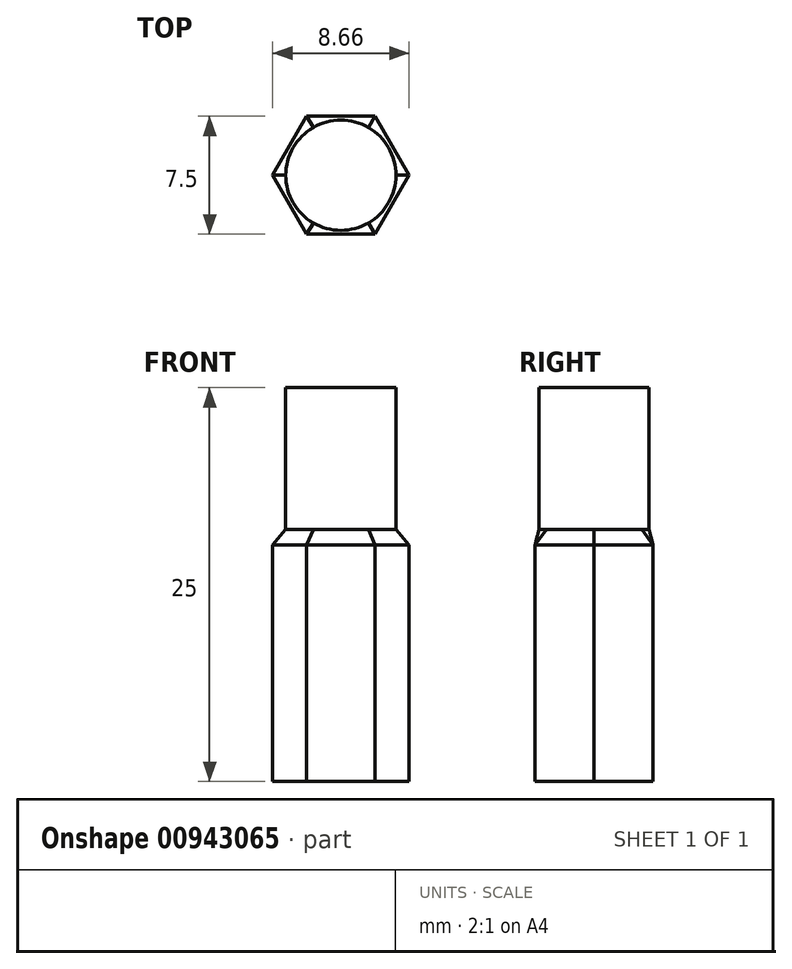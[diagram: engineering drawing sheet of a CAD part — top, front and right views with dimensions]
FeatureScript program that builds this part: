
annotation { "Feature Type Name" : "Feature", "Feature Type Description" : "" }
export const myFeature = defineFeature(function(context is Context, id is Id, definition is map)
    precondition{}
    {
        {
            var Q0;
            Q0=qCreatedBy(makeId("Top.planeOp"),FACE);
            var sketch = newSketch(context, id + "F0", { "sketchPlane" : qUnion([Q0])});
            skCircle(sketch, "E0.cCircle", {"center": v(0, 0) * mm, "radius": 3.75 * mm, "construction": true});
            skLineSegment(sketch, "E0.0", {"start": v(-2.17, 3.75) * mm, "end": v(2.17, 3.75) * mm});
            skLineSegment(sketch, "E0.1", {"start": v(2.17, 3.75) * mm, "end": v(4.33, 0) * mm});
            skLineSegment(sketch, "E0.2", {"start": v(4.33, 0) * mm, "end": v(2.17, -3.75) * mm});
            skLineSegment(sketch, "E0.3", {"start": v(2.17, -3.75) * mm, "end": v(-2.17, -3.75) * mm});
            skLineSegment(sketch, "E0.4", {"start": v(-2.17, -3.75) * mm, "end": v(-4.33, 0) * mm});
            skLineSegment(sketch, "E0.5", {"start": v(-4.33, 0) * mm, "end": v(-2.17, 3.75) * mm});
            skPoint(sketch, "E0.0.midPoint", {"position": v(0, 3.75) * mm});
            skSolve(sketch);
        }
        {
            var Q0;
            Q0=makeQuery(id+"F0.imprint","IMPRINT",FACE,{"disambiguationData":[TD([[makeQuery(id+"F0.imprint","IMPRINT",EDGE,{"derivedFrom":sQuery(id+"F0.wireOp",EDGE,"E0.0")}),-1.0]])]});
            extrude(context, id + "F1", {"entities" : qUnion([Q0]), "depth" : 15 * mm, "offsetDistance" : 25 * mm});
        }
        {
            var Q0;
            Q0=qCreatedBy(makeId("Top.planeOp"),FACE);
            cPlane(context, id + "F2", {"entities" : qUnion([Q0]), "cplaneType" : CPlaneType.OFFSET, "offset" : 16 * mm, "width" : 150 * mm, "height" : 150 * mm});
        }
        {
            var Q0;
            Q0=qCreatedBy(id+"F2.planeOp",FACE);
            var sketch = newSketch(context, id + "F3", { "sketchPlane" : qUnion([Q0])});
            skCircle(sketch, "E1", {"center": v(0, 0) * mm, "radius": 3.5 * mm});
            skSolve(sketch);
        }
        {
            var Q1;
            Q1=makeQuery(id+"F1.opExtrude","CAP_FACE",FACE,{"disambiguationData":[OSD([sQuery(id+"F0.wireOp",EDGE,"E0.0"),sQuery(id+"F0.wireOp",EDGE,"E0.1"),sQuery(id+"F0.wireOp",EDGE,"E0.2"),sQuery(id+"F0.wireOp",EDGE,"E0.3"),sQuery(id+"F0.wireOp",EDGE,"E0.4"),sQuery(id+"F0.wireOp",EDGE,"E0.5")])],"isStart":false});
            var Q2;
            Q2=makeQuery(id+"F3.imprint","IMPRINT",FACE,{"disambiguationData":[TD([[makeQuery(id+"F3.imprint","IMPRINT",EDGE,{"derivedFrom":sQuery(id+"F3.wireOp",EDGE,"E1")}),1.0]])]});
            loft(context, id + "F4", {"operationType" : NewBodyOperationType.ADD, "sheetProfilesArray" : [{ "sheetProfileEntities" : qUnion([Q1]) }, { "sheetProfileEntities" : qUnion([Q2]) }]});
        }
        {
            var Q0;
            Q0=makeQuery(id+"F4.opLoft","CAP_FACE",FACE,{"disambiguationData":[OSD([makeQuery(id+"F3.imprint","IMPRINT",FACE,{"disambiguationData":[TD([[makeQuery(id+"F3.imprint","IMPRINT",EDGE,{"derivedFrom":sQuery(id+"F3.wireOp",EDGE,"E1")}),1.0]])]})])],"isStart":true});
            extrude(context, id + "F5", {"entities" : qUnion([Q0]), "operationType" : NewBodyOperationType.ADD, "depth" : 9 * mm, "offsetDistance" : 25 * mm});
        }
    });
